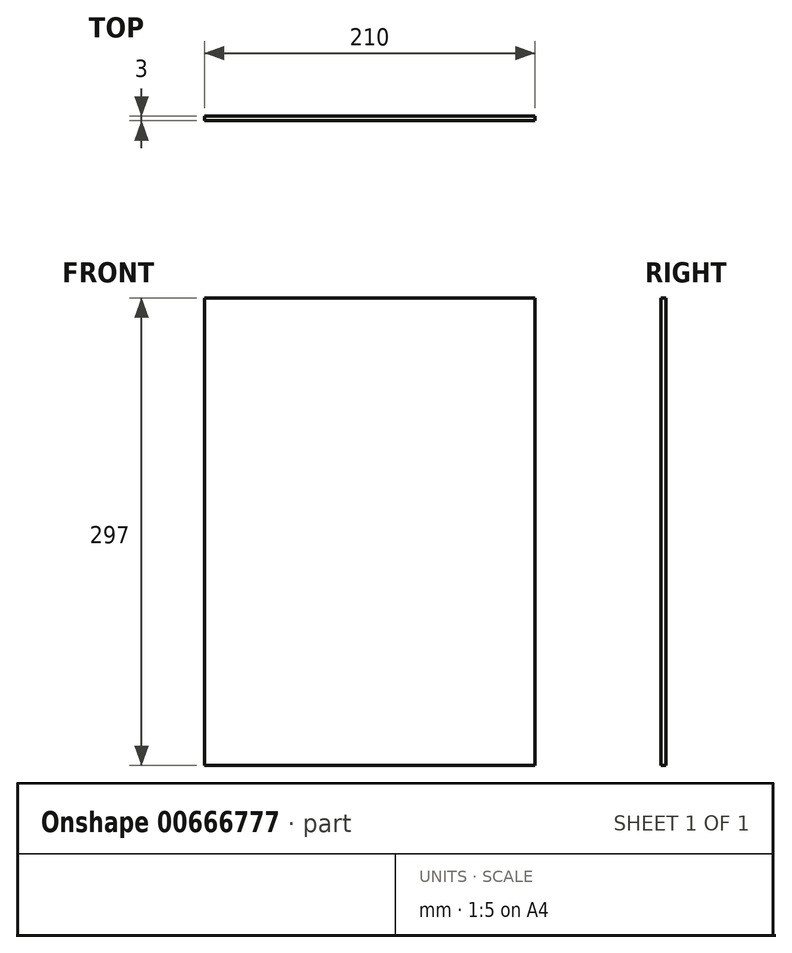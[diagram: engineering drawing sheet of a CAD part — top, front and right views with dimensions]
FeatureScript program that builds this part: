
annotation { "Feature Type Name" : "Feature", "Feature Type Description" : "" }
export const myFeature = defineFeature(function(context is Context, id is Id, definition is map)
    precondition{}
    {
        {
            var Q0;
            Q0=qCreatedBy(makeId("Front.planeOp"),FACE);
            var sketch = newSketch(context, id + "F0", { "sketchPlane" : qUnion([Q0])});
            skLineSegment(sketch, "E0.bottom", {"start": v(96.07, -139.15) * mm, "end": v(-113.93, -139.15) * mm});
            skLineSegment(sketch, "E0.top", {"start": v(96.07, 157.85) * mm, "end": v(-113.93, 157.85) * mm});
            skLineSegment(sketch, "E0.left", {"start": v(96.07, -139.15) * mm, "end": v(96.07, 157.85) * mm});
            skLineSegment(sketch, "E0.right", {"start": v(-113.93, -139.15) * mm, "end": v(-113.93, 157.85) * mm});
            skSolve(sketch);
        }
        {
            var Q0;
            Q0 = qSketchRegion(id + "F0", true);
            extrude(context, id + "F1", {"entities" : qUnion([Q0]), "depth" : 3 * mm, "offsetDistance" : 25 * mm});
        }
    });
